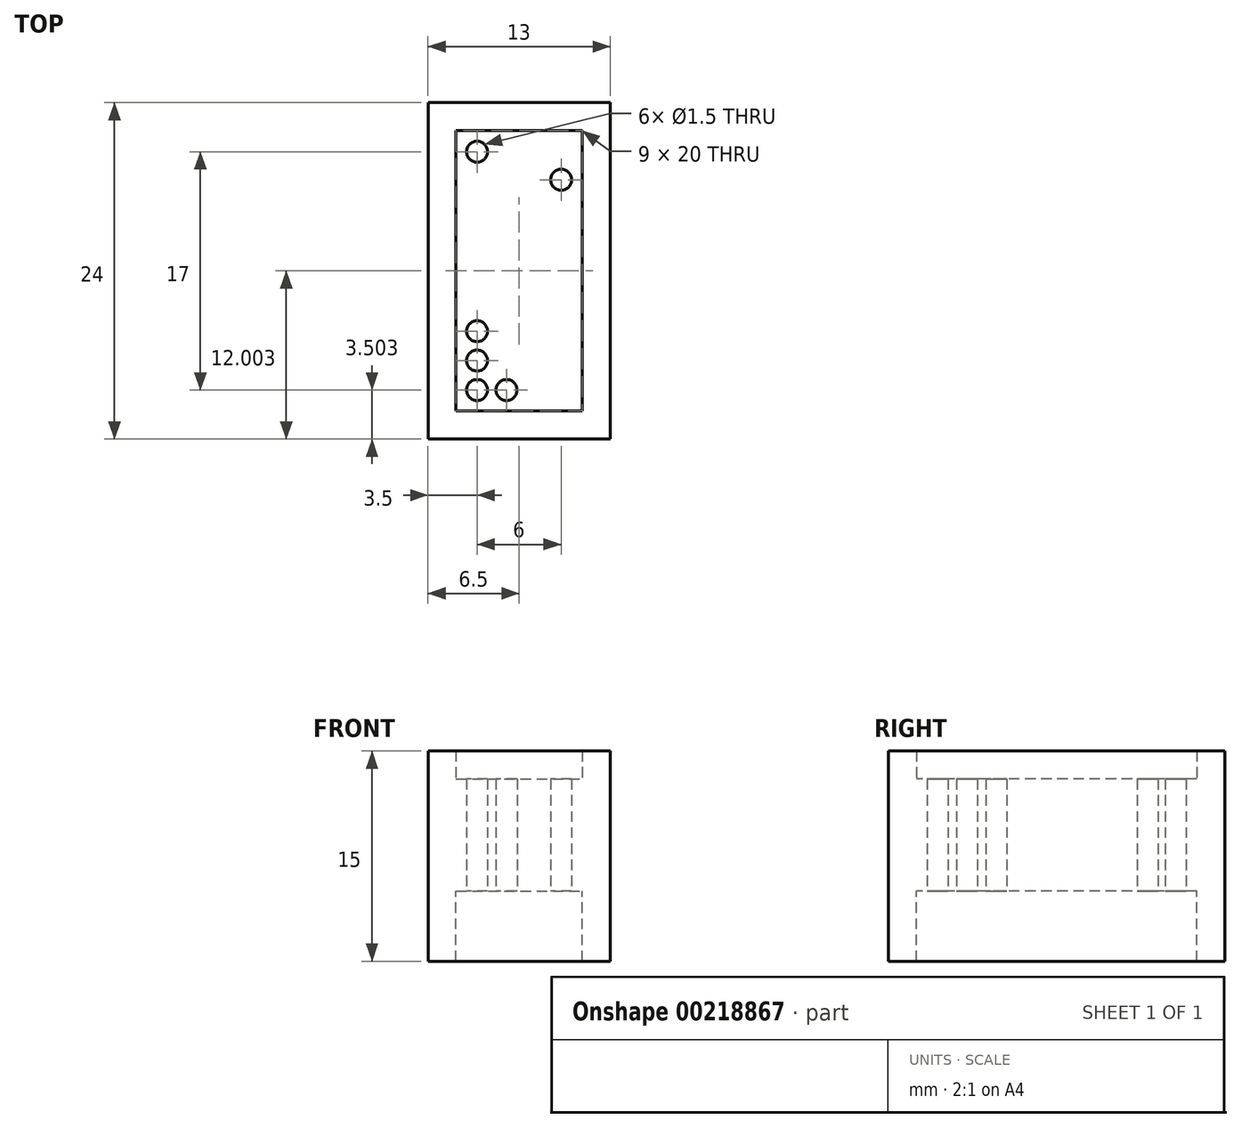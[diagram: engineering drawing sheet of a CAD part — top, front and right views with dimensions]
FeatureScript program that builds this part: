
annotation { "Feature Type Name" : "Feature", "Feature Type Description" : "" }
export const myFeature = defineFeature(function(context is Context, id is Id, definition is map)
    precondition{}
    {
        {
            var Q0;
            Q0=qCreatedBy(makeId("Top.planeOp"),FACE);
            var sketch = newSketch(context, id + "F0", { "sketchPlane" : qUnion([Q0])});
            skCircle(sketch, "E0", {"center": v(5.42, -13.1) * mm, "radius": 0.75 * mm});
            skCircle(sketch, "E1", {"center": v(7.52, -13.1) * mm, "radius": 0.75 * mm});
            skCircle(sketch, "E2", {"center": v(5.42, -11) * mm, "radius": 0.75 * mm});
            skCircle(sketch, "E3", {"center": v(5.42, -8.9) * mm, "radius": 0.75 * mm});
            skCircle(sketch, "E4", {"center": v(5.42, 3.9) * mm, "radius": 0.75 * mm});
            skCircle(sketch, "E5", {"center": v(11.42, 1.9) * mm, "radius": 0.75 * mm});
            skLineSegment(sketch, "E6.bottom", {"start": v(4.42, -14.1) * mm, "end": v(12.42, -14.1) * mm, "construction": true});
            skLineSegment(sketch, "E6.top", {"start": v(4.42, 4.9) * mm, "end": v(12.42, 4.9) * mm, "construction": true});
            skLineSegment(sketch, "E6.left", {"start": v(4.42, -14.1) * mm, "end": v(4.42, 4.9) * mm, "construction": true});
            skLineSegment(sketch, "E6.right", {"start": v(12.42, -14.1) * mm, "end": v(12.42, 4.9) * mm, "construction": true});
            skLineSegment(sketch, "E7.bottom", {"start": v(3.92, 5.4) * mm, "end": v(12.92, 5.4) * mm});
            skLineSegment(sketch, "E7.top", {"start": v(3.92, -14.6) * mm, "end": v(12.92, -14.6) * mm});
            skLineSegment(sketch, "E7.left", {"start": v(3.92, 5.4) * mm, "end": v(3.92, -14.6) * mm});
            skLineSegment(sketch, "E7.right", {"start": v(12.92, 5.4) * mm, "end": v(12.92, -14.6) * mm});
            skLineSegment(sketch, "E8.bottom", {"start": v(1.92, 7.4) * mm, "end": v(14.92, 7.4) * mm});
            skLineSegment(sketch, "E8.top", {"start": v(1.92, -16.6) * mm, "end": v(14.92, -16.6) * mm});
            skLineSegment(sketch, "E8.left", {"start": v(1.92, 7.4) * mm, "end": v(1.92, -16.6) * mm});
            skLineSegment(sketch, "E8.right", {"start": v(14.92, 7.4) * mm, "end": v(14.92, -16.6) * mm});
            skSolve(sketch);
        }
        {
            var Q0;
            Q0=makeQuery(id+"F0.imprint","IMPRINT",FACE,{"disambiguationData":[TD([[makeQuery(id+"F0.imprint","IMPRINT",EDGE,{"derivedFrom":sQuery(id+"F0.wireOp",EDGE,"E7.bottom")}),1.0]])]});
            var Q1;
            {var subQ0=sQuery(id+"F0.wireOp",EDGE,"E7.top");Q1=makeQuery(id+"F0.imprint","IMPRINT",FACE,{"disambiguationData":[TD([[makeQuery(id+"F0.imprint","IMPRINT",EDGE,{"derivedFrom":subQ0}),-1.0]])]});}
            extrude(context, id + "F1", {"entities" : qUnion([Q0, Q1]), "depth" : 10 * mm});
        }
        {
            var Q0;
            Q0=makeQuery(id+"F0.imprint","IMPRINT",FACE,{"disambiguationData":[TD([[makeQuery(id+"F0.imprint","IMPRINT",EDGE,{"derivedFrom":sQuery(id+"F0.wireOp",EDGE,"E0")}),-1.0]])]});
            var Q1;
            Q1=makeQuery(id+"F0.imprint","IMPRINT",FACE,{"disambiguationData":[TD([[makeQuery(id+"F0.imprint","IMPRINT",EDGE,{"derivedFrom":sQuery(id+"F0.wireOp",EDGE,"E7.bottom")}),1.0]])]});
            var Q2;
            {var subQ0=sQuery(id+"F0.wireOp",EDGE,"E7.top");Q2=makeQuery(id+"F0.imprint","IMPRINT",FACE,{"disambiguationData":[TD([[makeQuery(id+"F0.imprint","IMPRINT",EDGE,{"derivedFrom":subQ0}),-1.0]])]});}
            extrude(context, id + "F2", {"entities" : qUnion([Q0, Q1, Q2]), "operationType" : NewBodyOperationType.ADD, "depth" : 8 * mm});
        }
        {
            var Q0;
            Q0=makeQuery(id+"F0.imprint","IMPRINT",FACE,{"disambiguationData":[TD([[makeQuery(id+"F0.imprint","IMPRINT",EDGE,{"derivedFrom":sQuery(id+"F0.wireOp",EDGE,"E7.bottom")}),1.0]])]});
            var Q1;
            {var subQ0=sQuery(id+"F0.wireOp",EDGE,"E7.top");Q1=makeQuery(id+"F0.imprint","IMPRINT",FACE,{"disambiguationData":[TD([[makeQuery(id+"F0.imprint","IMPRINT",EDGE,{"derivedFrom":subQ0}),-1.0]])]});}
            extrude(context, id + "F3", {"entities" : qUnion([Q0, Q1]), "operationType" : NewBodyOperationType.ADD, "oppositeDirection" : true, "depth" : 5 * mm});
        }
    });
